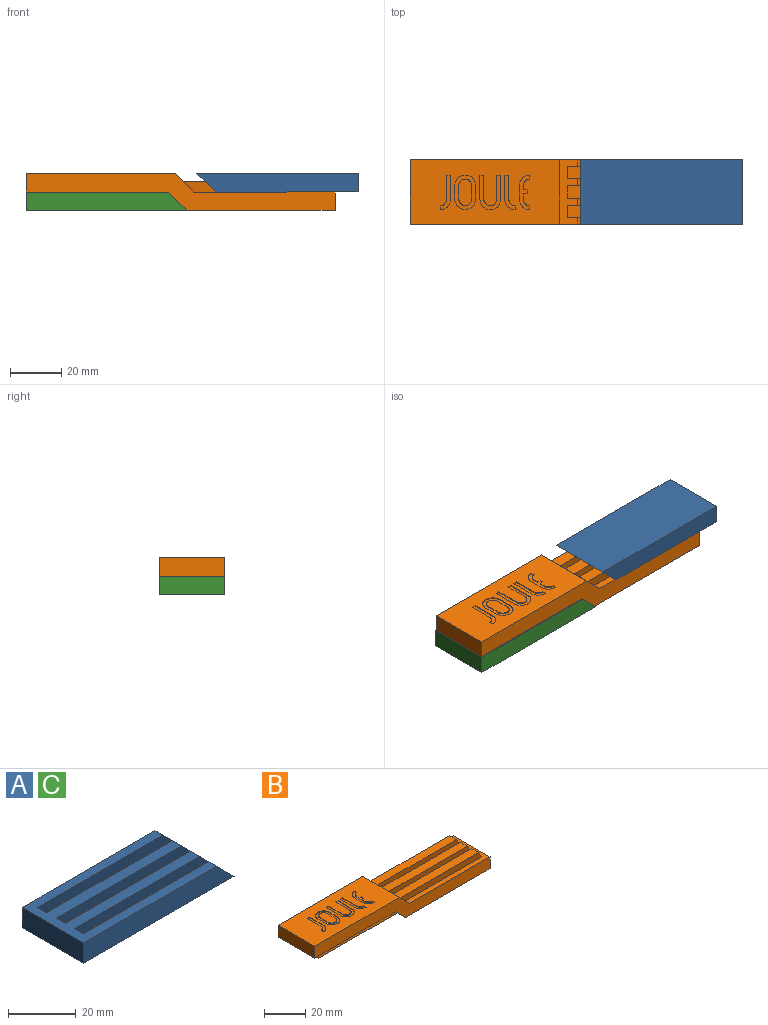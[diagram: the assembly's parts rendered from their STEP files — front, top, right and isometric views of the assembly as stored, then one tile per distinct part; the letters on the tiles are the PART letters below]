
ASSEMBLY  parts=3 mates=3
PART A: 18 faces, bbox 62.7x25.6x7.3 mm
  f0: plane 55.35x25.6mm, normal (0,0,1), area 823.6mm2, adj f1,f2,f3,f4,f7,f8,f9,f11
  f1: plane 62.65x7.3mm, normal (0,-1,0), area 430.7mm2, adj f0,f3,f4,f5
  f2: plane 62.65x7.3mm, normal (0,1,0), area 430.7mm2, adj f0,f3,f4,f5
  f3: plane 25.6x7.3mm, normal (-1,0,0), area 186.9mm2, adj f0,f1,f2,f5
  f4: plane 25.6x7.3mm, normal (0.71,0,0.71), area 191.5mm2, adj f0,f1,f2,f5,f6,f8,f9,f10
  f5: plane 62.65x25.6mm, normal (0,0,-1), area 1603.8mm2, adj f1,f2,f3,f4
  f6: plane 53.74x4.78mm, normal (0,0,1), area 257mm2, adj f4,f7,f8,f9
  f7: plane 4.78x4mm, normal (0.87,0,0.5), area 19.8mm2, adj f0,f6,f8,f9
  f8: plane 56.05x4mm, normal (0,-0.99,-0.12), area 213.2mm2, adj f0,f4,f6,f7
  f9: plane 56.05x4mm, normal (0,0.99,-0.12), area 213.2mm2, adj f0,f4,f6,f7
  f10: plane 53.74x4.78mm, normal (0,0,1), area 257mm2, adj f4,f11,f12,f13
  f11: plane 4.78x4mm, normal (0.87,0,0.5), area 19.8mm2, adj f0,f10,f12,f13
  f12: plane 56.05x4mm, normal (0,-0.99,-0.12), area 213.2mm2, adj f0,f4,f10,f11
  f13: plane 56.05x4mm, normal (0,0.99,-0.12), area 213.2mm2, adj f0,f4,f10,f11
  f14: plane 4.78x4mm, normal (0.87,0,0.5), area 19.8mm2, adj f0,f15,f16,f17
  f15: plane 53.74x4.78mm, normal (0,0,1), area 257mm2, adj f4,f14,f16,f17
  f16: plane 56.05x4mm, normal (0,0.99,-0.12), area 213.2mm2, adj f0,f4,f14,f15
  f17: plane 56.05x4mm, normal (0,-0.99,-0.12), area 213.2mm2, adj f0,f4,f14,f15
PART B: 126 faces, bbox 120x25x14 mm
  f0: plane 57.95x25mm, normal (0,0,-1), area 1238.2mm2, adj f10,f15,f16,f17,f80,f81,f82,f83
  f1: plane 57.95x25mm, normal (0,0,1), area 1238.2mm2, adj f12,f13,f16,f17,f34,f35,f36,f37
  f2: plane 4.78x4mm, normal (0.87,0,0.5), area 19.8mm2, adj f4,f11,f30,f33
  f3: plane 4.78x4mm, normal (0.87,0,0.5), area 19.8mm2, adj f5,f11,f24,f31
  f4: plane 53.74x4.78mm, normal (0,0,1), area 257mm2, adj f2,f12,f30,f33
  f5: plane 53.74x4.78mm, normal (0,0,1), area 257mm2, adj f3,f12,f24,f31
  f6: plane 4.78x4mm, normal (-0.87,0,-0.5), area 19.8mm2, adj f14,f20,f21,f28
  f7: plane 4.78x4mm, normal (-0.87,0,-0.5), area 19.8mm2, adj f8,f14,f26,f29
  f8: plane 53.74x4.78mm, normal (0,0,-1), area 257mm2, adj f7,f15,f26,f29
  f9: plane 53.74x4.78mm, normal (0,0,-1), area 257mm2, adj f15,f18,f19,f27
  f10: plane 25x7mm, normal (1,0,0), area 175mm2, adj f0,f11,f16,f17
  f11: plane 55.05x25mm, normal (0,0,1), area 782.9mm2, adj f2,f3,f10,f12,f16,f17,f22,f23
  f12: plane 25x7mm, normal (0.71,0,0.71), area 174.7mm2, adj f1,f4,f5,f11,f16,f17,f22,f24
  f13: plane 25x7mm, normal (-1,0,0), area 175mm2, adj f1,f14,f16,f17
  f14: plane 55.05x25mm, normal (0,0,-1), area 782.9mm2, adj f6,f7,f13,f15,f16,f17,f18,f19
  f15: plane 25x7mm, normal (-0.71,0,-0.71), area 174.7mm2, adj f0,f8,f9,f14,f16,f17,f18,f20
  f16: plane 120x14mm, normal (0,-1,0), area 860.3mm2, adj f0,f1,f10,f11,f12,f13,f14,f15
  f17: plane 120x14mm, normal (0,1,0), area 860.3mm2, adj f0,f1,f10,f11,f12,f13,f14,f15
  f18: plane 56.05x4mm, normal (0,-0.99,0.12), area 213.2mm2, adj f9,f14,f15,f19
  f19: plane 4.78x4mm, normal (-0.87,0,-0.5), area 19.8mm2, adj f9,f14,f18,f27
  f20: plane 56.05x4mm, normal (0,0.99,0.12), area 213.2mm2, adj f6,f14,f15,f21
  f21: plane 53.74x4.78mm, normal (0,0,-1), area 257mm2, adj f6,f15,f20,f28
  f22: plane 56.05x4mm, normal (0,-0.99,-0.12), area 213.2mm2, adj f11,f12,f23,f25
  f23: plane 4.78x4mm, normal (0.87,0,0.5), area 19.8mm2, adj f11,f22,f25,f32
  f24: plane 56.05x4mm, normal (0,0.99,-0.12), area 213.2mm2, adj f3,f5,f11,f12
  f25: plane 53.74x4.78mm, normal (0,0,1), area 257mm2, adj f12,f22,f23,f32
  f26: plane 56.05x4mm, normal (0,-0.99,0.12), area 213.2mm2, adj f7,f8,f14,f15
  f27: plane 56.05x4mm, normal (0,0.99,0.12), area 213.2mm2, adj f9,f14,f15,f19
  f28: plane 56.05x4mm, normal (0,-0.99,0.12), area 213.2mm2, adj f6,f14,f15,f21
  f29: plane 56.05x4mm, normal (0,0.99,0.12), area 213.2mm2, adj f7,f8,f14,f15
  f30: plane 56.05x4mm, normal (0,0.99,-0.12), area 213.2mm2, adj f2,f4,f11,f12
  f31: plane 56.05x4mm, normal (0,-0.99,-0.12), area 213.2mm2, adj f3,f5,f11,f12
  f32: plane 56.05x4mm, normal (0,0.99,-0.12), area 213.2mm2, adj f11,f12,f23,f25
  f33: plane 56.05x4mm, normal (0,-0.99,-0.12), area 213.2mm2, adj f2,f4,f11,f12
  f34: plane 9.45x0.3mm, normal (1,0,0), area 2.8mm2, adj f1,f35,f41,f42
  f35: cylinder r=4.01mm len=8.03mm, axis (0,0,1), area 3.8mm2, adj f1,f34,f36,f42
  f36: plane 9.45x0.3mm, normal (-1,0,0), area 2.8mm2, adj f1,f35,f37,f42
  f37: plane 1.55x0.3mm, normal (0,-1,0), area 0.5mm2, adj f1,f36,f38,f42
  f38: plane 9.45x0.3mm, normal (1,0,0), area 2.8mm2, adj f1,f37,f39,f42
  f39: cylinder r=2.46mm len=4.92mm, axis (0,0,1), area 2.3mm2, adj f1,f38,f40,f42
  f40: plane 9.45x0.3mm, normal (-1,0,0), area 2.8mm2, adj f1,f39,f41,f42
  f41: plane 1.55x0.3mm, normal (0,-1,0), area 0.5mm2, adj f1,f34,f40,f42
  f42: plane 13.46x8.03mm, normal (0,0,1), area 45.1mm2, adj f34,f35,f36,f37,f38,f39,f40,f41
  f43: plane 5.38x0.3mm, normal (1,0,0), area 1.6mm2, adj f1,f44,f50,f51
  f44: cylinder r=4.01mm len=8.03mm, axis (0,0,1), area 3.8mm2, adj f1,f43,f45,f51
  f45: plane 5.38x0.3mm, normal (-1,0,0), area 1.6mm2, adj f1,f44,f50,f51
  f46: cylinder r=2.46mm len=4.92mm, axis (0,0,1), area 2.3mm2, adj f47,f49,f51,f52
  f47: plane 5.38x0.3mm, normal (-1,0,0), area 1.6mm2, adj f46,f48,f51,f52
  f48: cylinder r=2.46mm len=4.92mm, axis (0,0,1), area 2.3mm2, adj f47,f49,f51,f52
  f49: plane 5.38x0.3mm, normal (1,0,0), area 1.6mm2, adj f46,f48,f51,f52
  f50: cylinder r=4.01mm len=8.03mm, axis (0,0,1), area 3.8mm2, adj f1,f43,f45,f51
  f51: plane 13.41x8.03mm, normal (0,0,1), area 48.3mm2, adj f43,f44,f45,f46,f47,f48,f49,f50
  f52: plane 10.3x4.92mm, normal (0,0,1), area 45.5mm2, adj f46,f47,f48,f49
  f53: cylinder r=4.01mm len=4.01mm, axis (0,0,1), area 1.9mm2, adj f1,f54,f64,f65
  f54: plane 1.55x0.3mm, normal (-1,0,0), area 0.5mm2, adj f1,f53,f55,f65
  f55: cylinder r=2.46mm len=2.46mm, axis (0,0,1), area 1.2mm2, adj f1,f54,f56,f65
  f56: plane 2.14x0.3mm, normal (-1,0,0), area 0.6mm2, adj f1,f55,f57,f65
  f57: plane 1.47x0.3mm, normal (0,1,0), area 0.4mm2, adj f1,f56,f58,f65
  f58: plane 1.55x0.3mm, normal (-1,0,0), area 0.5mm2, adj f1,f57,f59,f65
  f59: plane 1.47x0.3mm, normal (0,-1,0), area 0.4mm2, adj f1,f58,f60,f65
  f60: plane 1.74x0.3mm, normal (-1,0,0), area 0.5mm2, adj f1,f59,f61,f65
  f61: cylinder r=2.46mm len=2.46mm, axis (0,0,1), area 1.2mm2, adj f1,f60,f62,f65
  f62: plane 1.55x0.3mm, normal (-1,0,0), area 0.5mm2, adj f1,f61,f63,f65
  f63: cylinder r=4.01mm len=4.01mm, axis (0,0,1), area 1.9mm2, adj f1,f62,f64,f65
  f64: plane 5.44x0.3mm, normal (1,0,0), area 1.6mm2, adj f1,f53,f63,f65
  f65: plane 13.46x4.01mm, normal (0,0,1), area 26.5mm2, adj f53,f54,f55,f56,f57,f58,f59,f60
  f66: cylinder r=4.01mm len=4.01mm, axis (0,0,1), area 1.9mm2, adj f1,f67,f71,f72
  f67: plane 1.55x0.3mm, normal (-1,0,0), area 0.5mm2, adj f1,f66,f68,f72
  f68: cylinder r=2.46mm len=2.46mm, axis (0,0,1), area 1.2mm2, adj f1,f67,f69,f72
  f69: plane 9.45x0.3mm, normal (-1,0,0), area 2.8mm2, adj f1,f68,f70,f72
  f70: plane 1.55x0.3mm, normal (0,-1,0), area 0.5mm2, adj f1,f69,f71,f72
  f71: plane 9.45x0.3mm, normal (1,0,0), area 2.8mm2, adj f1,f66,f70,f72
  f72: plane 13.46x4.01mm, normal (0,0,1), area 22.6mm2, adj f66,f67,f68,f69,f70,f71
  f73: plane 9.45x0.3mm, normal (1,0,0), area 2.8mm2, adj f1,f74,f78,f79
  f74: cylinder r=2.46mm len=2.46mm, axis (0,0,1), area 1.2mm2, adj f1,f73,f75,f79
  f75: plane 1.55x0.3mm, normal (1,0,0), area 0.5mm2, adj f1,f74,f76,f79
  f76: cylinder r=4.01mm len=4.01mm, axis (0,0,1), area 1.9mm2, adj f1,f75,f77,f79
  f77: plane 9.45x0.3mm, normal (-1,0,0), area 2.8mm2, adj f1,f76,f78,f79
  f78: plane 1.55x0.3mm, normal (0,-1,0), area 0.5mm2, adj f1,f73,f77,f79
  f79: plane 13.46x4.01mm, normal (0,0,1), area 22.6mm2, adj f73,f74,f75,f76,f77,f78
  f80: plane 9.45x0.3mm, normal (1,0,0), area 2.8mm2, adj f0,f81,f87,f88
  f81: cylinder r=4.01mm len=8.03mm, axis (0,0,-1), area 3.8mm2, adj f0,f80,f82,f88
  f82: plane 9.45x0.3mm, normal (-1,0,0), area 2.8mm2, adj f0,f81,f83,f88
  f83: plane 1.55x0.3mm, normal (0,1,0), area 0.5mm2, adj f0,f82,f84,f88
  f84: plane 9.45x0.3mm, normal (1,0,0), area 2.8mm2, adj f0,f83,f85,f88
  f85: cylinder r=2.46mm len=4.92mm, axis (0,0,-1), area 2.3mm2, adj f0,f84,f86,f88
  f86: plane 9.45x0.3mm, normal (-1,0,0), area 2.8mm2, adj f0,f85,f87,f88
  f87: plane 1.55x0.3mm, normal (0,1,0), area 0.5mm2, adj f0,f80,f86,f88
  f88: plane 13.46x8.03mm, normal (0,0,-1), area 45.1mm2, adj f80,f81,f82,f83,f84,f85,f86,f87
  f89: plane 5.38x0.3mm, normal (1,0,0), area 1.6mm2, adj f0,f90,f96,f97
  f90: cylinder r=4.01mm len=8.03mm, axis (0,0,-1), area 3.8mm2, adj f0,f89,f91,f97
  f91: plane 5.38x0.3mm, normal (-1,0,0), area 1.6mm2, adj f0,f90,f96,f97
  f92: cylinder r=2.46mm len=4.92mm, axis (0,0,-1), area 2.3mm2, adj f93,f95,f97,f98
  f93: plane 5.38x0.3mm, normal (-1,0,0), area 1.6mm2, adj f92,f94,f97,f98
  f94: cylinder r=2.46mm len=4.92mm, axis (0,0,-1), area 2.3mm2, adj f93,f95,f97,f98
  f95: plane 5.38x0.3mm, normal (1,0,0), area 1.6mm2, adj f92,f94,f97,f98
  f96: cylinder r=4.01mm len=8.03mm, axis (0,0,-1), area 3.8mm2, adj f0,f89,f91,f97
  f97: plane 13.41x8.03mm, normal (0,0,-1), area 48.3mm2, adj f89,f90,f91,f92,f93,f94,f95,f96
  f98: plane 10.3x4.92mm, normal (0,0,-1), area 45.5mm2, adj f92,f93,f94,f95
  f99: cylinder r=4.01mm len=4.01mm, axis (0,0,-1), area 1.9mm2, adj f0,f100,f110,f111
  f100: plane 1.55x0.3mm, normal (-1,0,0), area 0.5mm2, adj f0,f99,f101,f111
  f101: cylinder r=2.46mm len=2.46mm, axis (0,0,-1), area 1.2mm2, adj f0,f100,f102,f111
  f102: plane 2.14x0.3mm, normal (-1,0,0), area 0.6mm2, adj f0,f101,f103,f111
  f103: plane 1.47x0.3mm, normal (0,-1,0), area 0.4mm2, adj f0,f102,f104,f111
  f104: plane 1.55x0.3mm, normal (-1,0,0), area 0.5mm2, adj f0,f103,f105,f111
  f105: plane 1.47x0.3mm, normal (0,1,0), area 0.4mm2, adj f0,f104,f106,f111
  f106: plane 1.74x0.3mm, normal (-1,0,0), area 0.5mm2, adj f0,f105,f107,f111
  f107: cylinder r=2.46mm len=2.46mm, axis (0,0,-1), area 1.2mm2, adj f0,f106,f108,f111
  f108: plane 1.55x0.3mm, normal (-1,0,0), area 0.5mm2, adj f0,f107,f109,f111
  f109: cylinder r=4.01mm len=4.01mm, axis (0,0,-1), area 1.9mm2, adj f0,f108,f110,f111
  f110: plane 5.44x0.3mm, normal (1,0,0), area 1.6mm2, adj f0,f99,f109,f111
  f111: plane 13.46x4.01mm, normal (0,0,-1), area 26.5mm2, adj f99,f100,f101,f102,f103,f104,f105,f106
  f112: cylinder r=4.01mm len=4.01mm, axis (0,0,-1), area 1.9mm2, adj f0,f113,f117,f118
  f113: plane 1.55x0.3mm, normal (-1,0,0), area 0.5mm2, adj f0,f112,f114,f118
  f114: cylinder r=2.46mm len=2.46mm, axis (0,0,-1), area 1.2mm2, adj f0,f113,f115,f118
  f115: plane 9.45x0.3mm, normal (-1,0,0), area 2.8mm2, adj f0,f114,f116,f118
  f116: plane 1.55x0.3mm, normal (0,1,0), area 0.5mm2, adj f0,f115,f117,f118
  f117: plane 9.45x0.3mm, normal (1,0,0), area 2.8mm2, adj f0,f112,f116,f118
  f118: plane 13.46x4.01mm, normal (0,0,-1), area 22.6mm2, adj f112,f113,f114,f115,f116,f117
  f119: plane 9.45x0.3mm, normal (1,0,0), area 2.8mm2, adj f0,f120,f124,f125
  f120: cylinder r=2.46mm len=2.46mm, axis (0,0,-1), area 1.2mm2, adj f0,f119,f121,f125
  f121: plane 1.55x0.3mm, normal (1,0,0), area 0.5mm2, adj f0,f120,f122,f125
  f122: cylinder r=4.01mm len=4.01mm, axis (0,0,-1), area 1.9mm2, adj f0,f121,f123,f125
  f123: plane 9.45x0.3mm, normal (-1,0,0), area 2.8mm2, adj f0,f122,f124,f125
  f124: plane 1.55x0.3mm, normal (0,1,0), area 0.5mm2, adj f0,f119,f123,f125
  f125: plane 13.46x4.01mm, normal (0,0,-1), area 22.6mm2, adj f119,f120,f121,f122,f123,f124
PART C: same geometry as A
PLACE A rot(axis=(0,1,0),180deg) t=(8.64,0,0)mm
PLACE B at identity fixed
PLACE C t=(0.2,0,0)mm
MATE fastened B.f14 <-> C.f0  axis (0,0,-1) through (-33.61,0,0)mm
MATE planar A.f16 <-> B.f33  axis (0,0.99,0.12) through (38.02,-2.15,2.01)mm
MATE planar A.f0 <-> B.f11  axis (0,0,-1) through (42.45,0,0)mm
